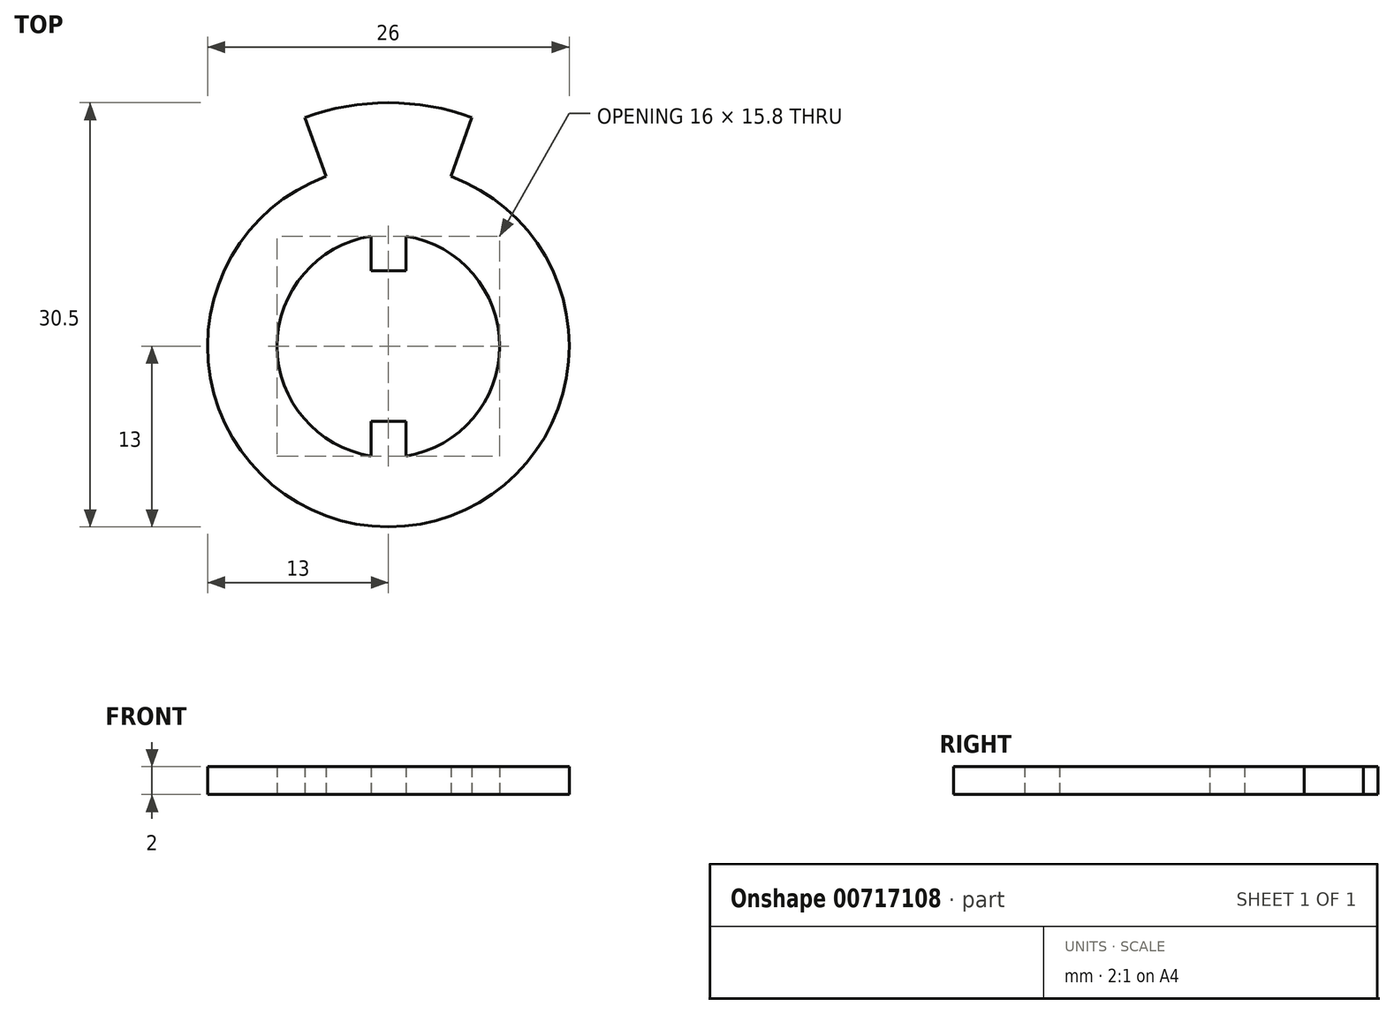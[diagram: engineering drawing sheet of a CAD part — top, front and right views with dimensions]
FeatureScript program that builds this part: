
annotation { "Feature Type Name" : "Feature", "Feature Type Description" : "" }
export const myFeature = defineFeature(function(context is Context, id is Id, definition is map)
    precondition{}
    {
        {
            var Q0;
            Q0=qCreatedBy(makeId("Top.planeOp"),FACE);
            var sketch = newSketch(context, id + "F0", { "sketchPlane" : qUnion([Q0])});
            skCircle(sketch, "E0", {"center": v(0, 0) * mm, "radius": 13 * mm});
            skArc(sketch, "E1", {"start": v(-1.25, 7.9) * mm, "mid": v(-8, 0) * mm, "end": v(-1.25, -7.9) * mm});
            skLineSegment(sketch, "E2.top", {"start": v(-1.25, 5.4) * mm, "end": v(1.25, 5.4) * mm});
            skLineSegment(sketch, "E2.left", {"start": v(-1.25, 7.9) * mm, "end": v(-1.25, 5.4) * mm});
            skLineSegment(sketch, "E2.right", {"start": v(1.25, 7.9) * mm, "end": v(1.25, 5.4) * mm});
            skLineSegment(sketch, "E3.MirrorCS", {"start": v(1.25, -7.9) * mm, "end": v(1.25, -5.4) * mm});
            skLineSegment(sketch, "E4.MirrorCS", {"start": v(-1.25, -7.9) * mm, "end": v(-1.25, -5.4) * mm});
            skLineSegment(sketch, "E5.MirrorCS", {"start": v(-1.25, -5.4) * mm, "end": v(1.25, -5.4) * mm});
            skArc(sketch, "E6.trimOffspring", {"start": v(1.25, -7.9) * mm, "mid": v(8, 0) * mm, "end": v(1.25, 7.9) * mm});
            skArc(sketch, "E7", {"start": v(6, 16.44) * mm, "mid": v(0, 17.5) * mm, "end": v(-6, 16.44) * mm});
            skLineSegment(sketch, "E8", {"start": v(-4.5, 12.2) * mm, "end": v(-6, 16.44) * mm});
            skLineSegment(sketch, "E9", {"start": v(4.5, 12.2) * mm, "end": v(6, 16.44) * mm});
            skSolve(sketch);
        }
        {
            var Q0;
            Q0 = qSketchRegion(id + "F0", true);
            extrude(context, id + "F1", {"entities" : qUnion([Q0]), "depth" : 2 * mm, "offsetDistance" : 25 * mm});
        }
    });
